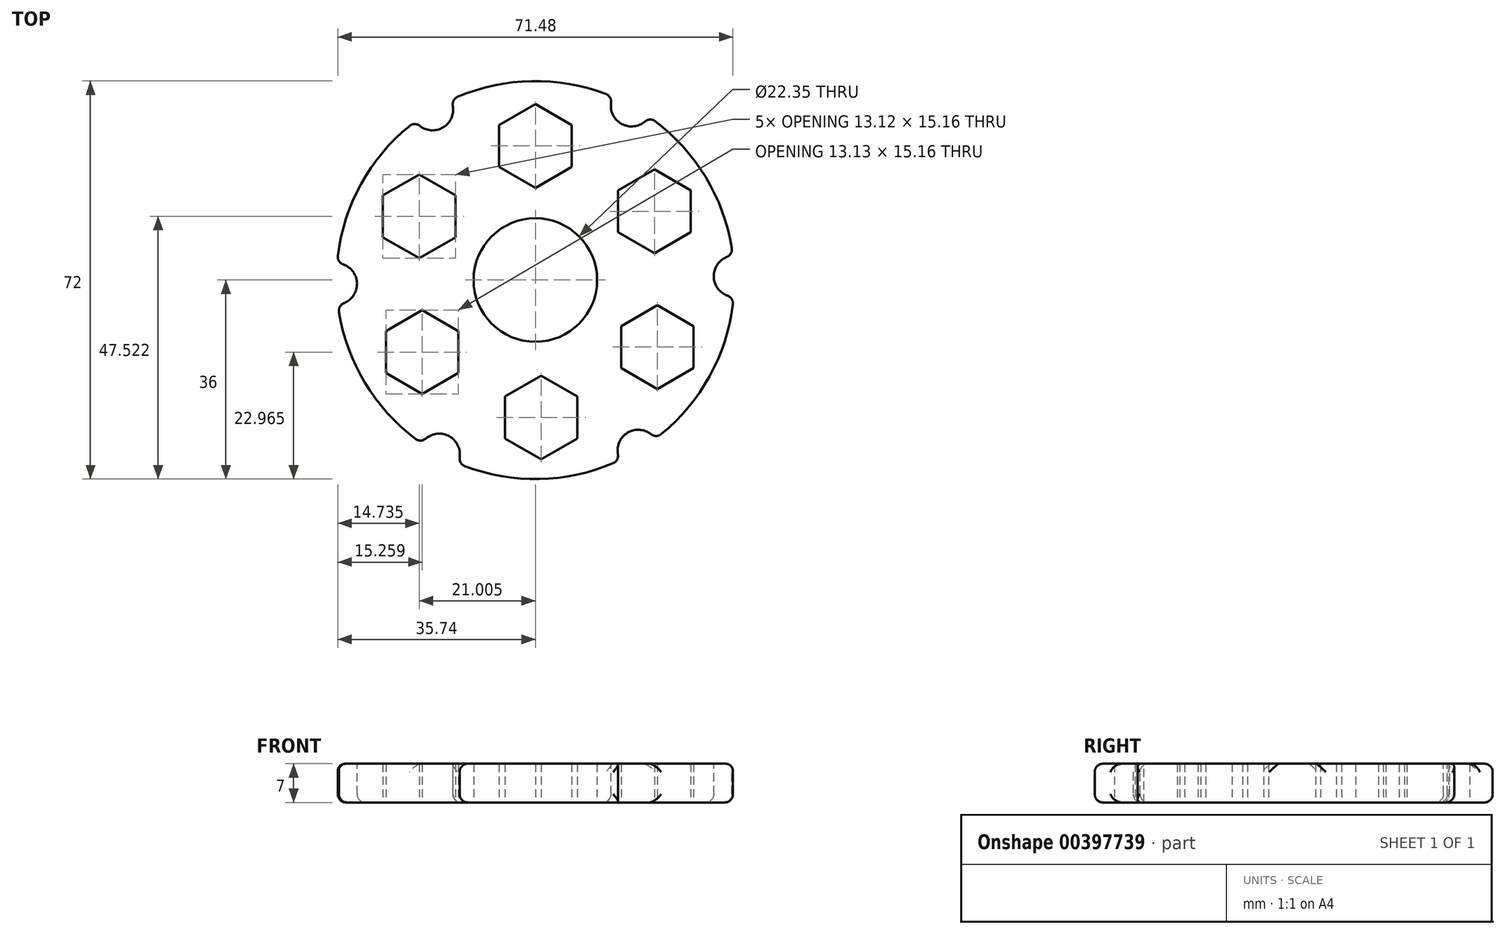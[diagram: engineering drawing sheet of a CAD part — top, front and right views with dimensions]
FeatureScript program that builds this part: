
annotation { "Feature Type Name" : "Feature", "Feature Type Description" : "" }
export const myFeature = defineFeature(function(context is Context, id is Id, definition is map)
    precondition{}
    {
        {
            var Q0;
            Q0=qCreatedBy(makeId("Top.planeOp"),FACE);
            var sketch = newSketch(context, id + "F0", { "sketchPlane" : qUnion([Q0])});
            skCircle(sketch, "E0", {"center": v(0, 0) * mm, "radius": 11.18 * mm});
            skCircle(sketch, "E1", {"center": v(0, 0) * mm, "radius": 36 * mm});
            skCircle(sketch, "E2.cCircle", {"center": v(0, 24.25) * mm, "radius": 6.56 * mm, "construction": true});
            skLineSegment(sketch, "E2.0", {"start": v(6.56, 28.04) * mm, "end": v(6.56, 20.47) * mm});
            skLineSegment(sketch, "E2.1", {"start": v(6.56, 20.47) * mm, "end": v(0, 16.68) * mm});
            skLineSegment(sketch, "E2.2", {"start": v(0, 16.68) * mm, "end": v(-6.56, 20.47) * mm});
            skLineSegment(sketch, "E2.3", {"start": v(-6.56, 20.47) * mm, "end": v(-6.56, 28.04) * mm});
            skLineSegment(sketch, "E2.4", {"start": v(-6.56, 28.04) * mm, "end": v(0, 31.83) * mm});
            skLineSegment(sketch, "E2.5", {"start": v(0, 31.83) * mm, "end": v(6.56, 28.04) * mm});
            skLineSegment(sketch, "E3.1.0", {"start": v(28.1, 8.64) * mm, "end": v(21.53, 4.85) * mm});
            skLineSegment(sketch, "E3.1.1", {"start": v(28.1, 16.22) * mm, "end": v(28.1, 8.64) * mm});
            skLineSegment(sketch, "E3.1.2", {"start": v(21.53, 20) * mm, "end": v(28.1, 16.22) * mm});
            skLineSegment(sketch, "E3.1.3", {"start": v(14.97, 16.22) * mm, "end": v(21.53, 20) * mm});
            skLineSegment(sketch, "E3.1.4", {"start": v(14.97, 8.64) * mm, "end": v(14.97, 16.22) * mm});
            skLineSegment(sketch, "E3.1.5", {"start": v(21.53, 4.85) * mm, "end": v(14.97, 8.64) * mm});
            skLineSegment(sketch, "E3.2.0", {"start": v(22.05, -19.7) * mm, "end": v(15.5, -15.92) * mm});
            skLineSegment(sketch, "E3.2.1", {"start": v(28.62, -15.92) * mm, "end": v(22.05, -19.7) * mm});
            skLineSegment(sketch, "E3.2.2", {"start": v(28.62, -8.34) * mm, "end": v(28.62, -15.92) * mm});
            skLineSegment(sketch, "E3.2.3", {"start": v(22.05, -4.55) * mm, "end": v(28.62, -8.34) * mm});
            skLineSegment(sketch, "E3.2.4", {"start": v(15.5, -8.34) * mm, "end": v(22.05, -4.55) * mm});
            skLineSegment(sketch, "E3.2.5", {"start": v(15.5, -15.92) * mm, "end": v(15.5, -8.34) * mm});
            skLineSegment(sketch, "E3.3.0", {"start": v(-5.51, -28.65) * mm, "end": v(-5.51, -21.07) * mm});
            skLineSegment(sketch, "E3.3.1", {"start": v(1.05, -32.44) * mm, "end": v(-5.51, -28.65) * mm});
            skLineSegment(sketch, "E3.3.2", {"start": v(7.61, -28.65) * mm, "end": v(1.05, -32.44) * mm});
            skLineSegment(sketch, "E3.3.3", {"start": v(7.61, -21.07) * mm, "end": v(7.61, -28.65) * mm});
            skLineSegment(sketch, "E3.3.4", {"start": v(1.05, -17.28) * mm, "end": v(7.61, -21.07) * mm});
            skLineSegment(sketch, "E3.3.5", {"start": v(-5.51, -21.07) * mm, "end": v(1.05, -17.28) * mm});
            skLineSegment(sketch, "E3.4.0", {"start": v(-27.04, -9.25) * mm, "end": v(-20.48, -5.46) * mm});
            skLineSegment(sketch, "E3.4.1", {"start": v(-27.04, -16.82) * mm, "end": v(-27.04, -9.25) * mm});
            skLineSegment(sketch, "E3.4.2", {"start": v(-20.48, -20.61) * mm, "end": v(-27.04, -16.82) * mm});
            skLineSegment(sketch, "E3.4.3", {"start": v(-13.92, -16.82) * mm, "end": v(-20.48, -20.61) * mm});
            skLineSegment(sketch, "E3.4.4", {"start": v(-13.92, -9.25) * mm, "end": v(-13.92, -16.82) * mm});
            skLineSegment(sketch, "E3.4.5", {"start": v(-20.48, -5.46) * mm, "end": v(-13.92, -9.25) * mm});
            skLineSegment(sketch, "E3.5.0", {"start": v(-21, 19.1) * mm, "end": v(-14.44, 15.31) * mm});
            skLineSegment(sketch, "E3.5.1", {"start": v(-27.57, 15.31) * mm, "end": v(-21, 19.1) * mm});
            skLineSegment(sketch, "E3.5.2", {"start": v(-27.57, 7.73) * mm, "end": v(-27.57, 15.31) * mm});
            skLineSegment(sketch, "E3.5.3", {"start": v(-21, 3.94) * mm, "end": v(-27.57, 7.73) * mm});
            skLineSegment(sketch, "E3.5.4", {"start": v(-14.44, 7.73) * mm, "end": v(-21, 3.94) * mm});
            skLineSegment(sketch, "E3.5.5", {"start": v(-14.44, 15.31) * mm, "end": v(-14.44, 7.73) * mm});
            skPoint(sketch, "E3.center", {"position": v(0.52, -0.3) * mm});
            skLineSegment(sketch, "E3.anchor1", {"start": v(0.52, -0.3) * mm, "end": v(6.56, 20.47) * mm, "construction": true});
            skLineSegment(sketch, "E3.anchor2", {"start": v(0.52, -0.3) * mm, "end": v(-14.44, 15.31) * mm, "construction": true});
            skSolve(sketch);
        }
        {
            var Q0;
            Q0=makeQuery(id+"F0.imprint","IMPRINT",FACE,{"disambiguationData":[TD([[makeQuery(id+"F0.imprint","IMPRINT",EDGE,{"derivedFrom":sQuery(id+"F0.wireOp",EDGE,"E0")}),-1.0]])]});
            extrude(context, id + "F1", {"entities" : qUnion([Q0]), "depth" : 7 * mm});
        }
        {
            var Q0;
            Q0=makeQuery(id+"F1.opExtrude","CAP_FACE",FACE,{"disambiguationData":[OSD([sQuery(id+"F0.wireOp",EDGE,"E0"),sQuery(id+"F0.wireOp",EDGE,"E1"),sQuery(id+"F0.wireOp",EDGE,"E2.0"),sQuery(id+"F0.wireOp",EDGE,"E2.1"),sQuery(id+"F0.wireOp",EDGE,"E2.2"),sQuery(id+"F0.wireOp",EDGE,"E2.3"),sQuery(id+"F0.wireOp",EDGE,"E2.4"),sQuery(id+"F0.wireOp",EDGE,"E2.5"),sQuery(id+"F0.wireOp",EDGE,"E3.1.0"),sQuery(id+"F0.wireOp",EDGE,"E3.1.1"),sQuery(id+"F0.wireOp",EDGE,"E3.1.2"),sQuery(id+"F0.wireOp",EDGE,"E3.1.3"),sQuery(id+"F0.wireOp",EDGE,"E3.1.4"),sQuery(id+"F0.wireOp",EDGE,"E3.1.5"),sQuery(id+"F0.wireOp",EDGE,"E3.2.0"),sQuery(id+"F0.wireOp",EDGE,"E3.2.1"),sQuery(id+"F0.wireOp",EDGE,"E3.2.2"),sQuery(id+"F0.wireOp",EDGE,"E3.2.3"),sQuery(id+"F0.wireOp",EDGE,"E3.2.4"),sQuery(id+"F0.wireOp",EDGE,"E3.2.5"),sQuery(id+"F0.wireOp",EDGE,"E3.3.0"),sQuery(id+"F0.wireOp",EDGE,"E3.3.1"),sQuery(id+"F0.wireOp",EDGE,"E3.3.2"),sQuery(id+"F0.wireOp",EDGE,"E3.3.3"),sQuery(id+"F0.wireOp",EDGE,"E3.3.4"),sQuery(id+"F0.wireOp",EDGE,"E3.3.5"),sQuery(id+"F0.wireOp",EDGE,"E3.4.0"),sQuery(id+"F0.wireOp",EDGE,"E3.4.1"),sQuery(id+"F0.wireOp",EDGE,"E3.4.2"),sQuery(id+"F0.wireOp",EDGE,"E3.4.3"),sQuery(id+"F0.wireOp",EDGE,"E3.4.4"),sQuery(id+"F0.wireOp",EDGE,"E3.4.5"),sQuery(id+"F0.wireOp",EDGE,"E3.5.0"),sQuery(id+"F0.wireOp",EDGE,"E3.5.1"),sQuery(id+"F0.wireOp",EDGE,"E3.5.2"),sQuery(id+"F0.wireOp",EDGE,"E3.5.3"),sQuery(id+"F0.wireOp",EDGE,"E3.5.4"),sQuery(id+"F0.wireOp",EDGE,"E3.5.5")])],"isStart":false});
            var sketch = newSketch(context, id + "F2", { "sketchPlane" : qUnion([Q0])});
            skCircle(sketch, "E4", {"center": v(17.4, 31.52) * mm, "radius": 3.73 * mm});
            skCircle(sketch, "E5.1.0", {"center": v(-18.6, 30.82) * mm, "radius": 3.73 * mm});
            skCircle(sketch, "E5.2.0", {"center": v(-36, -0.7) * mm, "radius": 3.73 * mm});
            skCircle(sketch, "E5.3.0", {"center": v(-17.4, -31.52) * mm, "radius": 3.73 * mm});
            skCircle(sketch, "E5.4.0", {"center": v(18.6, -30.82) * mm, "radius": 3.73 * mm});
            skCircle(sketch, "E5.5.0", {"center": v(36, 0.7) * mm, "radius": 3.73 * mm});
            skPoint(sketch, "E5.center", {"position": v(0, 0) * mm});
            skSolve(sketch);
        }
        {
            var Q0;
            {var subQ0=sQuery(id+"F2.wireOp",EDGE,"E5.1.0");var subQ1=makeQuery(id+"F1.opExtrude","CAP_EDGE",EDGE,{"disambiguationData":[OSD([sQuery(id+"F0.wireOp",EDGE,"E1")])],"isStart":false});var subQ2=makeQuery(id+"F2.imprint","INTERSECT",VERTEX,{"disambiguationData":[OD(0.0)],"derivedFrom":[subQ1,subQ0]});Q0=makeQuery(id+"F2.imprint","IMPRINT",FACE,{"disambiguationData":[TD([[makeQuery(id+"F2.imprint","IMPRINT",EDGE,{"disambiguationData":[TD([[subQ2,1.0]])],"derivedFrom":subQ0}),1.0]])]});}
            var Q1;
            {var subQ0=sQuery(id+"F2.wireOp",EDGE,"E5.1.0");var subQ1=makeQuery(id+"F1.opExtrude","CAP_EDGE",EDGE,{"disambiguationData":[OSD([sQuery(id+"F0.wireOp",EDGE,"E1")])],"isStart":false});var subQ2=makeQuery(id+"F2.imprint","INTERSECT",VERTEX,{"disambiguationData":[OD(0.0)],"derivedFrom":[subQ1,subQ0]});Q1=makeQuery(id+"F2.imprint","IMPRINT",FACE,{"disambiguationData":[TD([[makeQuery(id+"F2.imprint","IMPRINT",EDGE,{"disambiguationData":[TD([[subQ2,-1.0]])],"derivedFrom":subQ0}),1.0]])]});}
            var Q2;
            {var subQ0=sQuery(id+"F2.wireOp",EDGE,"E4");var subQ1=makeQuery(id+"F1.opExtrude","CAP_EDGE",EDGE,{"disambiguationData":[OSD([sQuery(id+"F0.wireOp",EDGE,"E1")])],"isStart":false});var subQ2=makeQuery(id+"F2.imprint","INTERSECT",VERTEX,{"disambiguationData":[OD(0.0)],"derivedFrom":[subQ1,subQ0]});Q2=makeQuery(id+"F2.imprint","IMPRINT",FACE,{"disambiguationData":[TD([[makeQuery(id+"F2.imprint","IMPRINT",EDGE,{"disambiguationData":[TD([[subQ2,1.0]])],"derivedFrom":subQ0}),1.0]])]});}
            var Q3;
            {var subQ0=sQuery(id+"F2.wireOp",EDGE,"E4");var subQ1=makeQuery(id+"F1.opExtrude","CAP_EDGE",EDGE,{"disambiguationData":[OSD([sQuery(id+"F0.wireOp",EDGE,"E1")])],"isStart":false});var subQ2=makeQuery(id+"F2.imprint","INTERSECT",VERTEX,{"disambiguationData":[OD(0.0)],"derivedFrom":[subQ1,subQ0]});Q3=makeQuery(id+"F2.imprint","IMPRINT",FACE,{"disambiguationData":[TD([[makeQuery(id+"F2.imprint","IMPRINT",EDGE,{"disambiguationData":[TD([[subQ2,-1.0]])],"derivedFrom":subQ0}),1.0]])]});}
            var Q4;
            {var subQ0=sQuery(id+"F2.wireOp",EDGE,"E5.5.0");var subQ1=makeQuery(id+"F1.opExtrude","CAP_EDGE",EDGE,{"disambiguationData":[OSD([sQuery(id+"F0.wireOp",EDGE,"E1")])],"isStart":false});var subQ2=makeQuery(id+"F2.imprint","INTERSECT",VERTEX,{"disambiguationData":[OD(0.0)],"derivedFrom":[subQ1,subQ0]});Q4=makeQuery(id+"F2.imprint","IMPRINT",FACE,{"disambiguationData":[TD([[makeQuery(id+"F2.imprint","IMPRINT",EDGE,{"disambiguationData":[TD([[subQ2,-1.0]])],"derivedFrom":subQ0}),1.0]])]});}
            var Q5;
            {var subQ0=sQuery(id+"F2.wireOp",EDGE,"E5.5.0");var subQ1=makeQuery(id+"F1.opExtrude","CAP_EDGE",EDGE,{"disambiguationData":[OSD([sQuery(id+"F0.wireOp",EDGE,"E1")])],"isStart":false});var subQ2=makeQuery(id+"F2.imprint","INTERSECT",VERTEX,{"disambiguationData":[OD(0.0)],"derivedFrom":[subQ1,subQ0]});Q5=makeQuery(id+"F2.imprint","IMPRINT",FACE,{"disambiguationData":[TD([[makeQuery(id+"F2.imprint","IMPRINT",EDGE,{"disambiguationData":[TD([[subQ2,1.0]])],"derivedFrom":subQ0}),1.0]])]});}
            var Q6;
            {var subQ0=sQuery(id+"F2.wireOp",EDGE,"E5.4.0");var subQ1=makeQuery(id+"F1.opExtrude","CAP_EDGE",EDGE,{"disambiguationData":[OSD([sQuery(id+"F0.wireOp",EDGE,"E1")])],"isStart":false});var subQ2=makeQuery(id+"F2.imprint","INTERSECT",VERTEX,{"disambiguationData":[OD(0.0)],"derivedFrom":[subQ1,subQ0]});Q6=makeQuery(id+"F2.imprint","IMPRINT",FACE,{"disambiguationData":[TD([[makeQuery(id+"F2.imprint","IMPRINT",EDGE,{"disambiguationData":[TD([[subQ2,-1.0]])],"derivedFrom":subQ0}),1.0]])]});}
            var Q7;
            {var subQ0=sQuery(id+"F2.wireOp",EDGE,"E5.4.0");var subQ1=makeQuery(id+"F1.opExtrude","CAP_EDGE",EDGE,{"disambiguationData":[OSD([sQuery(id+"F0.wireOp",EDGE,"E1")])],"isStart":false});var subQ2=makeQuery(id+"F2.imprint","INTERSECT",VERTEX,{"disambiguationData":[OD(0.0)],"derivedFrom":[subQ1,subQ0]});Q7=makeQuery(id+"F2.imprint","IMPRINT",FACE,{"disambiguationData":[TD([[makeQuery(id+"F2.imprint","IMPRINT",EDGE,{"disambiguationData":[TD([[subQ2,1.0]])],"derivedFrom":subQ0}),1.0]])]});}
            var Q8;
            {var subQ0=sQuery(id+"F2.wireOp",EDGE,"E5.3.0");var subQ1=makeQuery(id+"F1.opExtrude","CAP_EDGE",EDGE,{"disambiguationData":[OSD([sQuery(id+"F0.wireOp",EDGE,"E1")])],"isStart":false});var subQ2=makeQuery(id+"F2.imprint","INTERSECT",VERTEX,{"disambiguationData":[OD(0.0)],"derivedFrom":[subQ1,subQ0]});Q8=makeQuery(id+"F2.imprint","IMPRINT",FACE,{"disambiguationData":[TD([[makeQuery(id+"F2.imprint","IMPRINT",EDGE,{"disambiguationData":[TD([[subQ2,-1.0]])],"derivedFrom":subQ0}),1.0]])]});}
            var Q9;
            {var subQ0=sQuery(id+"F2.wireOp",EDGE,"E5.3.0");var subQ1=makeQuery(id+"F1.opExtrude","CAP_EDGE",EDGE,{"disambiguationData":[OSD([sQuery(id+"F0.wireOp",EDGE,"E1")])],"isStart":false});var subQ2=makeQuery(id+"F2.imprint","INTERSECT",VERTEX,{"disambiguationData":[OD(0.0)],"derivedFrom":[subQ1,subQ0]});Q9=makeQuery(id+"F2.imprint","IMPRINT",FACE,{"disambiguationData":[TD([[makeQuery(id+"F2.imprint","IMPRINT",EDGE,{"disambiguationData":[TD([[subQ2,1.0]])],"derivedFrom":subQ0}),1.0]])]});}
            var Q10;
            {var subQ0=sQuery(id+"F2.wireOp",EDGE,"E5.2.0");var subQ1=makeQuery(id+"F1.opExtrude","CAP_EDGE",EDGE,{"disambiguationData":[OSD([sQuery(id+"F0.wireOp",EDGE,"E1")])],"isStart":false});var subQ2=makeQuery(id+"F2.imprint","INTERSECT",VERTEX,{"disambiguationData":[OD(0.0)],"derivedFrom":[subQ1,subQ0]});Q10=makeQuery(id+"F2.imprint","IMPRINT",FACE,{"disambiguationData":[TD([[makeQuery(id+"F2.imprint","IMPRINT",EDGE,{"disambiguationData":[TD([[subQ2,1.0]])],"derivedFrom":subQ0}),1.0]])]});}
            var Q11;
            {var subQ0=sQuery(id+"F2.wireOp",EDGE,"E5.2.0");var subQ1=makeQuery(id+"F1.opExtrude","CAP_EDGE",EDGE,{"disambiguationData":[OSD([sQuery(id+"F0.wireOp",EDGE,"E1")])],"isStart":false});var subQ2=makeQuery(id+"F2.imprint","INTERSECT",VERTEX,{"disambiguationData":[OD(0.0)],"derivedFrom":[subQ1,subQ0]});Q11=makeQuery(id+"F2.imprint","IMPRINT",FACE,{"disambiguationData":[TD([[makeQuery(id+"F2.imprint","IMPRINT",EDGE,{"disambiguationData":[TD([[subQ2,-1.0]])],"derivedFrom":subQ0}),1.0]])]});}
            extrude(context, id + "F3", {"entities" : qUnion([Q0, Q1, Q2, Q3, Q4, Q5, Q6, Q7, Q8, Q9, Q10, Q11]), "operationType" : NewBodyOperationType.REMOVE, "oppositeDirection" : true, "depth" : 25 * mm});
        }
        {
            var Q0;
            {var subQ0=sQuery(id+"F0.wireOp",EDGE,"E1");Q0=makeQuery(id+"F3.boolean.opBoolean","SPLIT",EDGE,{"disambiguationData":[TD([makeQuery(id+"F1.opExtrude","CAP_FACE",FACE,{"disambiguationData":[OSD([sQuery(id+"F0.wireOp",EDGE,"E0"),subQ0,sQuery(id+"F0.wireOp",EDGE,"E2.0"),sQuery(id+"F0.wireOp",EDGE,"E2.1"),sQuery(id+"F0.wireOp",EDGE,"E2.2"),sQuery(id+"F0.wireOp",EDGE,"E2.3"),sQuery(id+"F0.wireOp",EDGE,"E2.4"),sQuery(id+"F0.wireOp",EDGE,"E2.5"),sQuery(id+"F0.wireOp",EDGE,"E3.1.0"),sQuery(id+"F0.wireOp",EDGE,"E3.1.1"),sQuery(id+"F0.wireOp",EDGE,"E3.1.2"),sQuery(id+"F0.wireOp",EDGE,"E3.1.3"),sQuery(id+"F0.wireOp",EDGE,"E3.1.4"),sQuery(id+"F0.wireOp",EDGE,"E3.1.5"),sQuery(id+"F0.wireOp",EDGE,"E3.2.0"),sQuery(id+"F0.wireOp",EDGE,"E3.2.1"),sQuery(id+"F0.wireOp",EDGE,"E3.2.2"),sQuery(id+"F0.wireOp",EDGE,"E3.2.3"),sQuery(id+"F0.wireOp",EDGE,"E3.2.4"),sQuery(id+"F0.wireOp",EDGE,"E3.2.5"),sQuery(id+"F0.wireOp",EDGE,"E3.3.0"),sQuery(id+"F0.wireOp",EDGE,"E3.3.1"),sQuery(id+"F0.wireOp",EDGE,"E3.3.2"),sQuery(id+"F0.wireOp",EDGE,"E3.3.3"),sQuery(id+"F0.wireOp",EDGE,"E3.3.4"),sQuery(id+"F0.wireOp",EDGE,"E3.3.5"),sQuery(id+"F0.wireOp",EDGE,"E3.4.0"),sQuery(id+"F0.wireOp",EDGE,"E3.4.1"),sQuery(id+"F0.wireOp",EDGE,"E3.4.2"),sQuery(id+"F0.wireOp",EDGE,"E3.4.3"),sQuery(id+"F0.wireOp",EDGE,"E3.4.4"),sQuery(id+"F0.wireOp",EDGE,"E3.4.5"),sQuery(id+"F0.wireOp",EDGE,"E3.5.0"),sQuery(id+"F0.wireOp",EDGE,"E3.5.1"),sQuery(id+"F0.wireOp",EDGE,"E3.5.2"),sQuery(id+"F0.wireOp",EDGE,"E3.5.3"),sQuery(id+"F0.wireOp",EDGE,"E3.5.4"),sQuery(id+"F0.wireOp",EDGE,"E3.5.5")])],"isStart":false}),makeQuery(id+"F1.opExtrude","SWEPT_FACE",FACE,{"disambiguationData":[OSD([subQ0])]}),makeQuery(id+"F3.opExtrude","SWEPT_FACE",FACE,{"disambiguationData":[OSD([sQuery(id+"F2.wireOp",EDGE,"E5.1.0")])]}),makeQuery(id+"F3.opExtrude","SWEPT_FACE",FACE,{"disambiguationData":[OSD([sQuery(id+"F2.wireOp",EDGE,"E5.2.0")])]})])],"derivedFrom":makeQuery(id+"F1.opExtrude","CAP_EDGE",EDGE,{"disambiguationData":[OSD([subQ0])],"isStart":false})});}
            var Q1;
            Q1=makeQuery(id+"F3.boolean.opBoolean","COPY",EDGE,{"derivedFrom":makeQuery(id+"F3.opExtrude","CAP_EDGE",EDGE,{"disambiguationData":[OSD([sQuery(id+"F2.wireOp",EDGE,"E5.1.0")])],"isStart":true})});
            var Q2;
            {var subQ0=sQuery(id+"F0.wireOp",EDGE,"E1");Q2=makeQuery(id+"F3.boolean.opBoolean","SPLIT",EDGE,{"disambiguationData":[TD([makeQuery(id+"F1.opExtrude","CAP_FACE",FACE,{"disambiguationData":[OSD([sQuery(id+"F0.wireOp",EDGE,"E0"),subQ0,sQuery(id+"F0.wireOp",EDGE,"E2.0"),sQuery(id+"F0.wireOp",EDGE,"E2.1"),sQuery(id+"F0.wireOp",EDGE,"E2.2"),sQuery(id+"F0.wireOp",EDGE,"E2.3"),sQuery(id+"F0.wireOp",EDGE,"E2.4"),sQuery(id+"F0.wireOp",EDGE,"E2.5"),sQuery(id+"F0.wireOp",EDGE,"E3.1.0"),sQuery(id+"F0.wireOp",EDGE,"E3.1.1"),sQuery(id+"F0.wireOp",EDGE,"E3.1.2"),sQuery(id+"F0.wireOp",EDGE,"E3.1.3"),sQuery(id+"F0.wireOp",EDGE,"E3.1.4"),sQuery(id+"F0.wireOp",EDGE,"E3.1.5"),sQuery(id+"F0.wireOp",EDGE,"E3.2.0"),sQuery(id+"F0.wireOp",EDGE,"E3.2.1"),sQuery(id+"F0.wireOp",EDGE,"E3.2.2"),sQuery(id+"F0.wireOp",EDGE,"E3.2.3"),sQuery(id+"F0.wireOp",EDGE,"E3.2.4"),sQuery(id+"F0.wireOp",EDGE,"E3.2.5"),sQuery(id+"F0.wireOp",EDGE,"E3.3.0"),sQuery(id+"F0.wireOp",EDGE,"E3.3.1"),sQuery(id+"F0.wireOp",EDGE,"E3.3.2"),sQuery(id+"F0.wireOp",EDGE,"E3.3.3"),sQuery(id+"F0.wireOp",EDGE,"E3.3.4"),sQuery(id+"F0.wireOp",EDGE,"E3.3.5"),sQuery(id+"F0.wireOp",EDGE,"E3.4.0"),sQuery(id+"F0.wireOp",EDGE,"E3.4.1"),sQuery(id+"F0.wireOp",EDGE,"E3.4.2"),sQuery(id+"F0.wireOp",EDGE,"E3.4.3"),sQuery(id+"F0.wireOp",EDGE,"E3.4.4"),sQuery(id+"F0.wireOp",EDGE,"E3.4.5"),sQuery(id+"F0.wireOp",EDGE,"E3.5.0"),sQuery(id+"F0.wireOp",EDGE,"E3.5.1"),sQuery(id+"F0.wireOp",EDGE,"E3.5.2"),sQuery(id+"F0.wireOp",EDGE,"E3.5.3"),sQuery(id+"F0.wireOp",EDGE,"E3.5.4"),sQuery(id+"F0.wireOp",EDGE,"E3.5.5")])],"isStart":false}),makeQuery(id+"F1.opExtrude","SWEPT_FACE",FACE,{"disambiguationData":[OSD([subQ0])]}),makeQuery(id+"F3.opExtrude","SWEPT_FACE",FACE,{"disambiguationData":[OSD([sQuery(id+"F2.wireOp",EDGE,"E4")])]}),makeQuery(id+"F3.opExtrude","SWEPT_FACE",FACE,{"disambiguationData":[OSD([sQuery(id+"F2.wireOp",EDGE,"E5.1.0")])]})])],"derivedFrom":makeQuery(id+"F1.opExtrude","CAP_EDGE",EDGE,{"disambiguationData":[OSD([subQ0])],"isStart":false})});}
            var Q3;
            Q3=makeQuery(id+"F3.boolean.opBoolean","COPY",EDGE,{"derivedFrom":makeQuery(id+"F3.opExtrude","CAP_EDGE",EDGE,{"disambiguationData":[OSD([sQuery(id+"F2.wireOp",EDGE,"E4")])],"isStart":true})});
            var Q4;
            {var subQ0=sQuery(id+"F0.wireOp",EDGE,"E1");Q4=makeQuery(id+"F3.boolean.opBoolean","SPLIT",EDGE,{"disambiguationData":[TD([makeQuery(id+"F1.opExtrude","CAP_FACE",FACE,{"disambiguationData":[OSD([sQuery(id+"F0.wireOp",EDGE,"E0"),subQ0,sQuery(id+"F0.wireOp",EDGE,"E2.0"),sQuery(id+"F0.wireOp",EDGE,"E2.1"),sQuery(id+"F0.wireOp",EDGE,"E2.2"),sQuery(id+"F0.wireOp",EDGE,"E2.3"),sQuery(id+"F0.wireOp",EDGE,"E2.4"),sQuery(id+"F0.wireOp",EDGE,"E2.5"),sQuery(id+"F0.wireOp",EDGE,"E3.1.0"),sQuery(id+"F0.wireOp",EDGE,"E3.1.1"),sQuery(id+"F0.wireOp",EDGE,"E3.1.2"),sQuery(id+"F0.wireOp",EDGE,"E3.1.3"),sQuery(id+"F0.wireOp",EDGE,"E3.1.4"),sQuery(id+"F0.wireOp",EDGE,"E3.1.5"),sQuery(id+"F0.wireOp",EDGE,"E3.2.0"),sQuery(id+"F0.wireOp",EDGE,"E3.2.1"),sQuery(id+"F0.wireOp",EDGE,"E3.2.2"),sQuery(id+"F0.wireOp",EDGE,"E3.2.3"),sQuery(id+"F0.wireOp",EDGE,"E3.2.4"),sQuery(id+"F0.wireOp",EDGE,"E3.2.5"),sQuery(id+"F0.wireOp",EDGE,"E3.3.0"),sQuery(id+"F0.wireOp",EDGE,"E3.3.1"),sQuery(id+"F0.wireOp",EDGE,"E3.3.2"),sQuery(id+"F0.wireOp",EDGE,"E3.3.3"),sQuery(id+"F0.wireOp",EDGE,"E3.3.4"),sQuery(id+"F0.wireOp",EDGE,"E3.3.5"),sQuery(id+"F0.wireOp",EDGE,"E3.4.0"),sQuery(id+"F0.wireOp",EDGE,"E3.4.1"),sQuery(id+"F0.wireOp",EDGE,"E3.4.2"),sQuery(id+"F0.wireOp",EDGE,"E3.4.3"),sQuery(id+"F0.wireOp",EDGE,"E3.4.4"),sQuery(id+"F0.wireOp",EDGE,"E3.4.5"),sQuery(id+"F0.wireOp",EDGE,"E3.5.0"),sQuery(id+"F0.wireOp",EDGE,"E3.5.1"),sQuery(id+"F0.wireOp",EDGE,"E3.5.2"),sQuery(id+"F0.wireOp",EDGE,"E3.5.3"),sQuery(id+"F0.wireOp",EDGE,"E3.5.4"),sQuery(id+"F0.wireOp",EDGE,"E3.5.5")])],"isStart":false}),makeQuery(id+"F1.opExtrude","SWEPT_FACE",FACE,{"disambiguationData":[OSD([subQ0])]}),makeQuery(id+"F3.opExtrude","SWEPT_FACE",FACE,{"disambiguationData":[OSD([sQuery(id+"F2.wireOp",EDGE,"E4")])]}),makeQuery(id+"F3.opExtrude","SWEPT_FACE",FACE,{"disambiguationData":[OSD([sQuery(id+"F2.wireOp",EDGE,"E5.5.0")])]})])],"derivedFrom":makeQuery(id+"F1.opExtrude","CAP_EDGE",EDGE,{"disambiguationData":[OSD([subQ0])],"isStart":false})});}
            var Q5;
            Q5=makeQuery(id+"F3.boolean.opBoolean","COPY",EDGE,{"derivedFrom":makeQuery(id+"F3.opExtrude","CAP_EDGE",EDGE,{"disambiguationData":[OSD([sQuery(id+"F2.wireOp",EDGE,"E5.5.0")])],"isStart":true})});
            var Q6;
            {var subQ0=sQuery(id+"F0.wireOp",EDGE,"E1");Q6=makeQuery(id+"F3.boolean.opBoolean","SPLIT",EDGE,{"disambiguationData":[TD([makeQuery(id+"F1.opExtrude","CAP_FACE",FACE,{"disambiguationData":[OSD([sQuery(id+"F0.wireOp",EDGE,"E0"),subQ0,sQuery(id+"F0.wireOp",EDGE,"E2.0"),sQuery(id+"F0.wireOp",EDGE,"E2.1"),sQuery(id+"F0.wireOp",EDGE,"E2.2"),sQuery(id+"F0.wireOp",EDGE,"E2.3"),sQuery(id+"F0.wireOp",EDGE,"E2.4"),sQuery(id+"F0.wireOp",EDGE,"E2.5"),sQuery(id+"F0.wireOp",EDGE,"E3.1.0"),sQuery(id+"F0.wireOp",EDGE,"E3.1.1"),sQuery(id+"F0.wireOp",EDGE,"E3.1.2"),sQuery(id+"F0.wireOp",EDGE,"E3.1.3"),sQuery(id+"F0.wireOp",EDGE,"E3.1.4"),sQuery(id+"F0.wireOp",EDGE,"E3.1.5"),sQuery(id+"F0.wireOp",EDGE,"E3.2.0"),sQuery(id+"F0.wireOp",EDGE,"E3.2.1"),sQuery(id+"F0.wireOp",EDGE,"E3.2.2"),sQuery(id+"F0.wireOp",EDGE,"E3.2.3"),sQuery(id+"F0.wireOp",EDGE,"E3.2.4"),sQuery(id+"F0.wireOp",EDGE,"E3.2.5"),sQuery(id+"F0.wireOp",EDGE,"E3.3.0"),sQuery(id+"F0.wireOp",EDGE,"E3.3.1"),sQuery(id+"F0.wireOp",EDGE,"E3.3.2"),sQuery(id+"F0.wireOp",EDGE,"E3.3.3"),sQuery(id+"F0.wireOp",EDGE,"E3.3.4"),sQuery(id+"F0.wireOp",EDGE,"E3.3.5"),sQuery(id+"F0.wireOp",EDGE,"E3.4.0"),sQuery(id+"F0.wireOp",EDGE,"E3.4.1"),sQuery(id+"F0.wireOp",EDGE,"E3.4.2"),sQuery(id+"F0.wireOp",EDGE,"E3.4.3"),sQuery(id+"F0.wireOp",EDGE,"E3.4.4"),sQuery(id+"F0.wireOp",EDGE,"E3.4.5"),sQuery(id+"F0.wireOp",EDGE,"E3.5.0"),sQuery(id+"F0.wireOp",EDGE,"E3.5.1"),sQuery(id+"F0.wireOp",EDGE,"E3.5.2"),sQuery(id+"F0.wireOp",EDGE,"E3.5.3"),sQuery(id+"F0.wireOp",EDGE,"E3.5.4"),sQuery(id+"F0.wireOp",EDGE,"E3.5.5")])],"isStart":false}),makeQuery(id+"F1.opExtrude","SWEPT_FACE",FACE,{"disambiguationData":[OSD([subQ0])]}),makeQuery(id+"F3.opExtrude","SWEPT_FACE",FACE,{"disambiguationData":[OSD([sQuery(id+"F2.wireOp",EDGE,"E5.4.0")])]}),makeQuery(id+"F3.opExtrude","SWEPT_FACE",FACE,{"disambiguationData":[OSD([sQuery(id+"F2.wireOp",EDGE,"E5.5.0")])]})])],"derivedFrom":makeQuery(id+"F1.opExtrude","CAP_EDGE",EDGE,{"disambiguationData":[OSD([subQ0])],"isStart":false})});}
            var Q7;
            Q7=makeQuery(id+"F3.boolean.opBoolean","COPY",EDGE,{"derivedFrom":makeQuery(id+"F3.opExtrude","CAP_EDGE",EDGE,{"disambiguationData":[OSD([sQuery(id+"F2.wireOp",EDGE,"E5.4.0")])],"isStart":true})});
            var Q8;
            {var subQ0=sQuery(id+"F0.wireOp",EDGE,"E1");Q8=makeQuery(id+"F3.boolean.opBoolean","SPLIT",EDGE,{"disambiguationData":[TD([makeQuery(id+"F1.opExtrude","CAP_FACE",FACE,{"disambiguationData":[OSD([sQuery(id+"F0.wireOp",EDGE,"E0"),subQ0,sQuery(id+"F0.wireOp",EDGE,"E2.0"),sQuery(id+"F0.wireOp",EDGE,"E2.1"),sQuery(id+"F0.wireOp",EDGE,"E2.2"),sQuery(id+"F0.wireOp",EDGE,"E2.3"),sQuery(id+"F0.wireOp",EDGE,"E2.4"),sQuery(id+"F0.wireOp",EDGE,"E2.5"),sQuery(id+"F0.wireOp",EDGE,"E3.1.0"),sQuery(id+"F0.wireOp",EDGE,"E3.1.1"),sQuery(id+"F0.wireOp",EDGE,"E3.1.2"),sQuery(id+"F0.wireOp",EDGE,"E3.1.3"),sQuery(id+"F0.wireOp",EDGE,"E3.1.4"),sQuery(id+"F0.wireOp",EDGE,"E3.1.5"),sQuery(id+"F0.wireOp",EDGE,"E3.2.0"),sQuery(id+"F0.wireOp",EDGE,"E3.2.1"),sQuery(id+"F0.wireOp",EDGE,"E3.2.2"),sQuery(id+"F0.wireOp",EDGE,"E3.2.3"),sQuery(id+"F0.wireOp",EDGE,"E3.2.4"),sQuery(id+"F0.wireOp",EDGE,"E3.2.5"),sQuery(id+"F0.wireOp",EDGE,"E3.3.0"),sQuery(id+"F0.wireOp",EDGE,"E3.3.1"),sQuery(id+"F0.wireOp",EDGE,"E3.3.2"),sQuery(id+"F0.wireOp",EDGE,"E3.3.3"),sQuery(id+"F0.wireOp",EDGE,"E3.3.4"),sQuery(id+"F0.wireOp",EDGE,"E3.3.5"),sQuery(id+"F0.wireOp",EDGE,"E3.4.0"),sQuery(id+"F0.wireOp",EDGE,"E3.4.1"),sQuery(id+"F0.wireOp",EDGE,"E3.4.2"),sQuery(id+"F0.wireOp",EDGE,"E3.4.3"),sQuery(id+"F0.wireOp",EDGE,"E3.4.4"),sQuery(id+"F0.wireOp",EDGE,"E3.4.5"),sQuery(id+"F0.wireOp",EDGE,"E3.5.0"),sQuery(id+"F0.wireOp",EDGE,"E3.5.1"),sQuery(id+"F0.wireOp",EDGE,"E3.5.2"),sQuery(id+"F0.wireOp",EDGE,"E3.5.3"),sQuery(id+"F0.wireOp",EDGE,"E3.5.4"),sQuery(id+"F0.wireOp",EDGE,"E3.5.5")])],"isStart":false}),makeQuery(id+"F1.opExtrude","SWEPT_FACE",FACE,{"disambiguationData":[OSD([subQ0])]}),makeQuery(id+"F3.opExtrude","SWEPT_FACE",FACE,{"disambiguationData":[OSD([sQuery(id+"F2.wireOp",EDGE,"E5.3.0")])]}),makeQuery(id+"F3.opExtrude","SWEPT_FACE",FACE,{"disambiguationData":[OSD([sQuery(id+"F2.wireOp",EDGE,"E5.4.0")])]})])],"derivedFrom":makeQuery(id+"F1.opExtrude","CAP_EDGE",EDGE,{"disambiguationData":[OSD([subQ0])],"isStart":false})});}
            var Q9;
            Q9=makeQuery(id+"F3.boolean.opBoolean","COPY",EDGE,{"derivedFrom":makeQuery(id+"F3.opExtrude","CAP_EDGE",EDGE,{"disambiguationData":[OSD([sQuery(id+"F2.wireOp",EDGE,"E5.3.0")])],"isStart":true})});
            var Q10;
            {var subQ0=sQuery(id+"F0.wireOp",EDGE,"E1");Q10=makeQuery(id+"F3.boolean.opBoolean","SPLIT",EDGE,{"disambiguationData":[TD([makeQuery(id+"F1.opExtrude","CAP_FACE",FACE,{"disambiguationData":[OSD([sQuery(id+"F0.wireOp",EDGE,"E0"),subQ0,sQuery(id+"F0.wireOp",EDGE,"E2.0"),sQuery(id+"F0.wireOp",EDGE,"E2.1"),sQuery(id+"F0.wireOp",EDGE,"E2.2"),sQuery(id+"F0.wireOp",EDGE,"E2.3"),sQuery(id+"F0.wireOp",EDGE,"E2.4"),sQuery(id+"F0.wireOp",EDGE,"E2.5"),sQuery(id+"F0.wireOp",EDGE,"E3.1.0"),sQuery(id+"F0.wireOp",EDGE,"E3.1.1"),sQuery(id+"F0.wireOp",EDGE,"E3.1.2"),sQuery(id+"F0.wireOp",EDGE,"E3.1.3"),sQuery(id+"F0.wireOp",EDGE,"E3.1.4"),sQuery(id+"F0.wireOp",EDGE,"E3.1.5"),sQuery(id+"F0.wireOp",EDGE,"E3.2.0"),sQuery(id+"F0.wireOp",EDGE,"E3.2.1"),sQuery(id+"F0.wireOp",EDGE,"E3.2.2"),sQuery(id+"F0.wireOp",EDGE,"E3.2.3"),sQuery(id+"F0.wireOp",EDGE,"E3.2.4"),sQuery(id+"F0.wireOp",EDGE,"E3.2.5"),sQuery(id+"F0.wireOp",EDGE,"E3.3.0"),sQuery(id+"F0.wireOp",EDGE,"E3.3.1"),sQuery(id+"F0.wireOp",EDGE,"E3.3.2"),sQuery(id+"F0.wireOp",EDGE,"E3.3.3"),sQuery(id+"F0.wireOp",EDGE,"E3.3.4"),sQuery(id+"F0.wireOp",EDGE,"E3.3.5"),sQuery(id+"F0.wireOp",EDGE,"E3.4.0"),sQuery(id+"F0.wireOp",EDGE,"E3.4.1"),sQuery(id+"F0.wireOp",EDGE,"E3.4.2"),sQuery(id+"F0.wireOp",EDGE,"E3.4.3"),sQuery(id+"F0.wireOp",EDGE,"E3.4.4"),sQuery(id+"F0.wireOp",EDGE,"E3.4.5"),sQuery(id+"F0.wireOp",EDGE,"E3.5.0"),sQuery(id+"F0.wireOp",EDGE,"E3.5.1"),sQuery(id+"F0.wireOp",EDGE,"E3.5.2"),sQuery(id+"F0.wireOp",EDGE,"E3.5.3"),sQuery(id+"F0.wireOp",EDGE,"E3.5.4"),sQuery(id+"F0.wireOp",EDGE,"E3.5.5")])],"isStart":false}),makeQuery(id+"F1.opExtrude","SWEPT_FACE",FACE,{"disambiguationData":[OSD([subQ0])]}),makeQuery(id+"F3.opExtrude","SWEPT_FACE",FACE,{"disambiguationData":[OSD([sQuery(id+"F2.wireOp",EDGE,"E5.2.0")])]}),makeQuery(id+"F3.opExtrude","SWEPT_FACE",FACE,{"disambiguationData":[OSD([sQuery(id+"F2.wireOp",EDGE,"E5.3.0")])]})])],"derivedFrom":makeQuery(id+"F1.opExtrude","CAP_EDGE",EDGE,{"disambiguationData":[OSD([subQ0])],"isStart":false})});}
            var Q11;
            Q11=makeQuery(id+"F3.boolean.opBoolean","COPY",EDGE,{"derivedFrom":makeQuery(id+"F3.opExtrude","CAP_EDGE",EDGE,{"disambiguationData":[OSD([sQuery(id+"F2.wireOp",EDGE,"E5.2.0")])],"isStart":true})});
            var Q12;
            {var subQ0=sQuery(id+"F0.wireOp",EDGE,"E1");Q12=makeQuery(id+"F3.boolean.opBoolean","SPLIT",EDGE,{"disambiguationData":[TD([makeQuery(id+"F1.opExtrude","CAP_FACE",FACE,{"disambiguationData":[OSD([sQuery(id+"F0.wireOp",EDGE,"E0"),subQ0,sQuery(id+"F0.wireOp",EDGE,"E2.0"),sQuery(id+"F0.wireOp",EDGE,"E2.1"),sQuery(id+"F0.wireOp",EDGE,"E2.2"),sQuery(id+"F0.wireOp",EDGE,"E2.3"),sQuery(id+"F0.wireOp",EDGE,"E2.4"),sQuery(id+"F0.wireOp",EDGE,"E2.5"),sQuery(id+"F0.wireOp",EDGE,"E3.1.0"),sQuery(id+"F0.wireOp",EDGE,"E3.1.1"),sQuery(id+"F0.wireOp",EDGE,"E3.1.2"),sQuery(id+"F0.wireOp",EDGE,"E3.1.3"),sQuery(id+"F0.wireOp",EDGE,"E3.1.4"),sQuery(id+"F0.wireOp",EDGE,"E3.1.5"),sQuery(id+"F0.wireOp",EDGE,"E3.2.0"),sQuery(id+"F0.wireOp",EDGE,"E3.2.1"),sQuery(id+"F0.wireOp",EDGE,"E3.2.2"),sQuery(id+"F0.wireOp",EDGE,"E3.2.3"),sQuery(id+"F0.wireOp",EDGE,"E3.2.4"),sQuery(id+"F0.wireOp",EDGE,"E3.2.5"),sQuery(id+"F0.wireOp",EDGE,"E3.3.0"),sQuery(id+"F0.wireOp",EDGE,"E3.3.1"),sQuery(id+"F0.wireOp",EDGE,"E3.3.2"),sQuery(id+"F0.wireOp",EDGE,"E3.3.3"),sQuery(id+"F0.wireOp",EDGE,"E3.3.4"),sQuery(id+"F0.wireOp",EDGE,"E3.3.5"),sQuery(id+"F0.wireOp",EDGE,"E3.4.0"),sQuery(id+"F0.wireOp",EDGE,"E3.4.1"),sQuery(id+"F0.wireOp",EDGE,"E3.4.2"),sQuery(id+"F0.wireOp",EDGE,"E3.4.3"),sQuery(id+"F0.wireOp",EDGE,"E3.4.4"),sQuery(id+"F0.wireOp",EDGE,"E3.4.5"),sQuery(id+"F0.wireOp",EDGE,"E3.5.0"),sQuery(id+"F0.wireOp",EDGE,"E3.5.1"),sQuery(id+"F0.wireOp",EDGE,"E3.5.2"),sQuery(id+"F0.wireOp",EDGE,"E3.5.3"),sQuery(id+"F0.wireOp",EDGE,"E3.5.4"),sQuery(id+"F0.wireOp",EDGE,"E3.5.5")])],"isStart":true}),makeQuery(id+"F1.opExtrude","SWEPT_FACE",FACE,{"disambiguationData":[OSD([subQ0])]}),makeQuery(id+"F3.opExtrude","SWEPT_FACE",FACE,{"disambiguationData":[OSD([sQuery(id+"F2.wireOp",EDGE,"E5.4.0")])]}),makeQuery(id+"F3.opExtrude","SWEPT_FACE",FACE,{"disambiguationData":[OSD([sQuery(id+"F2.wireOp",EDGE,"E5.5.0")])]})])],"derivedFrom":makeQuery(id+"F1.opExtrude","CAP_EDGE",EDGE,{"disambiguationData":[OSD([subQ0])],"isStart":true})});}
            var Q13;
            Q13=makeQuery(id+"F3.boolean.opBoolean","INTERSECT",EDGE,{"derivedFrom":[makeQuery(id+"F1.opExtrude","CAP_FACE",FACE,{"disambiguationData":[OSD([sQuery(id+"F0.wireOp",EDGE,"E0"),sQuery(id+"F0.wireOp",EDGE,"E1"),sQuery(id+"F0.wireOp",EDGE,"E2.0"),sQuery(id+"F0.wireOp",EDGE,"E2.1"),sQuery(id+"F0.wireOp",EDGE,"E2.2"),sQuery(id+"F0.wireOp",EDGE,"E2.3"),sQuery(id+"F0.wireOp",EDGE,"E2.4"),sQuery(id+"F0.wireOp",EDGE,"E2.5"),sQuery(id+"F0.wireOp",EDGE,"E3.1.0"),sQuery(id+"F0.wireOp",EDGE,"E3.1.1"),sQuery(id+"F0.wireOp",EDGE,"E3.1.2"),sQuery(id+"F0.wireOp",EDGE,"E3.1.3"),sQuery(id+"F0.wireOp",EDGE,"E3.1.4"),sQuery(id+"F0.wireOp",EDGE,"E3.1.5"),sQuery(id+"F0.wireOp",EDGE,"E3.2.0"),sQuery(id+"F0.wireOp",EDGE,"E3.2.1"),sQuery(id+"F0.wireOp",EDGE,"E3.2.2"),sQuery(id+"F0.wireOp",EDGE,"E3.2.3"),sQuery(id+"F0.wireOp",EDGE,"E3.2.4"),sQuery(id+"F0.wireOp",EDGE,"E3.2.5"),sQuery(id+"F0.wireOp",EDGE,"E3.3.0"),sQuery(id+"F0.wireOp",EDGE,"E3.3.1"),sQuery(id+"F0.wireOp",EDGE,"E3.3.2"),sQuery(id+"F0.wireOp",EDGE,"E3.3.3"),sQuery(id+"F0.wireOp",EDGE,"E3.3.4"),sQuery(id+"F0.wireOp",EDGE,"E3.3.5"),sQuery(id+"F0.wireOp",EDGE,"E3.4.0"),sQuery(id+"F0.wireOp",EDGE,"E3.4.1"),sQuery(id+"F0.wireOp",EDGE,"E3.4.2"),sQuery(id+"F0.wireOp",EDGE,"E3.4.3"),sQuery(id+"F0.wireOp",EDGE,"E3.4.4"),sQuery(id+"F0.wireOp",EDGE,"E3.4.5"),sQuery(id+"F0.wireOp",EDGE,"E3.5.0"),sQuery(id+"F0.wireOp",EDGE,"E3.5.1"),sQuery(id+"F0.wireOp",EDGE,"E3.5.2"),sQuery(id+"F0.wireOp",EDGE,"E3.5.3"),sQuery(id+"F0.wireOp",EDGE,"E3.5.4"),sQuery(id+"F0.wireOp",EDGE,"E3.5.5")])],"isStart":true}),makeQuery(id+"F3.opExtrude","SWEPT_FACE",FACE,{"disambiguationData":[OSD([sQuery(id+"F2.wireOp",EDGE,"E5.5.0")])]})]});
            var Q14;
            {var subQ0=sQuery(id+"F0.wireOp",EDGE,"E1");Q14=makeQuery(id+"F3.boolean.opBoolean","SPLIT",EDGE,{"disambiguationData":[TD([makeQuery(id+"F1.opExtrude","CAP_FACE",FACE,{"disambiguationData":[OSD([sQuery(id+"F0.wireOp",EDGE,"E0"),subQ0,sQuery(id+"F0.wireOp",EDGE,"E2.0"),sQuery(id+"F0.wireOp",EDGE,"E2.1"),sQuery(id+"F0.wireOp",EDGE,"E2.2"),sQuery(id+"F0.wireOp",EDGE,"E2.3"),sQuery(id+"F0.wireOp",EDGE,"E2.4"),sQuery(id+"F0.wireOp",EDGE,"E2.5"),sQuery(id+"F0.wireOp",EDGE,"E3.1.0"),sQuery(id+"F0.wireOp",EDGE,"E3.1.1"),sQuery(id+"F0.wireOp",EDGE,"E3.1.2"),sQuery(id+"F0.wireOp",EDGE,"E3.1.3"),sQuery(id+"F0.wireOp",EDGE,"E3.1.4"),sQuery(id+"F0.wireOp",EDGE,"E3.1.5"),sQuery(id+"F0.wireOp",EDGE,"E3.2.0"),sQuery(id+"F0.wireOp",EDGE,"E3.2.1"),sQuery(id+"F0.wireOp",EDGE,"E3.2.2"),sQuery(id+"F0.wireOp",EDGE,"E3.2.3"),sQuery(id+"F0.wireOp",EDGE,"E3.2.4"),sQuery(id+"F0.wireOp",EDGE,"E3.2.5"),sQuery(id+"F0.wireOp",EDGE,"E3.3.0"),sQuery(id+"F0.wireOp",EDGE,"E3.3.1"),sQuery(id+"F0.wireOp",EDGE,"E3.3.2"),sQuery(id+"F0.wireOp",EDGE,"E3.3.3"),sQuery(id+"F0.wireOp",EDGE,"E3.3.4"),sQuery(id+"F0.wireOp",EDGE,"E3.3.5"),sQuery(id+"F0.wireOp",EDGE,"E3.4.0"),sQuery(id+"F0.wireOp",EDGE,"E3.4.1"),sQuery(id+"F0.wireOp",EDGE,"E3.4.2"),sQuery(id+"F0.wireOp",EDGE,"E3.4.3"),sQuery(id+"F0.wireOp",EDGE,"E3.4.4"),sQuery(id+"F0.wireOp",EDGE,"E3.4.5"),sQuery(id+"F0.wireOp",EDGE,"E3.5.0"),sQuery(id+"F0.wireOp",EDGE,"E3.5.1"),sQuery(id+"F0.wireOp",EDGE,"E3.5.2"),sQuery(id+"F0.wireOp",EDGE,"E3.5.3"),sQuery(id+"F0.wireOp",EDGE,"E3.5.4"),sQuery(id+"F0.wireOp",EDGE,"E3.5.5")])],"isStart":true}),makeQuery(id+"F1.opExtrude","SWEPT_FACE",FACE,{"disambiguationData":[OSD([subQ0])]}),makeQuery(id+"F3.opExtrude","SWEPT_FACE",FACE,{"disambiguationData":[OSD([sQuery(id+"F2.wireOp",EDGE,"E4")])]}),makeQuery(id+"F3.opExtrude","SWEPT_FACE",FACE,{"disambiguationData":[OSD([sQuery(id+"F2.wireOp",EDGE,"E5.5.0")])]})])],"derivedFrom":makeQuery(id+"F1.opExtrude","CAP_EDGE",EDGE,{"disambiguationData":[OSD([subQ0])],"isStart":true})});}
            var Q15;
            Q15=makeQuery(id+"F3.boolean.opBoolean","INTERSECT",EDGE,{"derivedFrom":[makeQuery(id+"F1.opExtrude","CAP_FACE",FACE,{"disambiguationData":[OSD([sQuery(id+"F0.wireOp",EDGE,"E0"),sQuery(id+"F0.wireOp",EDGE,"E1"),sQuery(id+"F0.wireOp",EDGE,"E2.0"),sQuery(id+"F0.wireOp",EDGE,"E2.1"),sQuery(id+"F0.wireOp",EDGE,"E2.2"),sQuery(id+"F0.wireOp",EDGE,"E2.3"),sQuery(id+"F0.wireOp",EDGE,"E2.4"),sQuery(id+"F0.wireOp",EDGE,"E2.5"),sQuery(id+"F0.wireOp",EDGE,"E3.1.0"),sQuery(id+"F0.wireOp",EDGE,"E3.1.1"),sQuery(id+"F0.wireOp",EDGE,"E3.1.2"),sQuery(id+"F0.wireOp",EDGE,"E3.1.3"),sQuery(id+"F0.wireOp",EDGE,"E3.1.4"),sQuery(id+"F0.wireOp",EDGE,"E3.1.5"),sQuery(id+"F0.wireOp",EDGE,"E3.2.0"),sQuery(id+"F0.wireOp",EDGE,"E3.2.1"),sQuery(id+"F0.wireOp",EDGE,"E3.2.2"),sQuery(id+"F0.wireOp",EDGE,"E3.2.3"),sQuery(id+"F0.wireOp",EDGE,"E3.2.4"),sQuery(id+"F0.wireOp",EDGE,"E3.2.5"),sQuery(id+"F0.wireOp",EDGE,"E3.3.0"),sQuery(id+"F0.wireOp",EDGE,"E3.3.1"),sQuery(id+"F0.wireOp",EDGE,"E3.3.2"),sQuery(id+"F0.wireOp",EDGE,"E3.3.3"),sQuery(id+"F0.wireOp",EDGE,"E3.3.4"),sQuery(id+"F0.wireOp",EDGE,"E3.3.5"),sQuery(id+"F0.wireOp",EDGE,"E3.4.0"),sQuery(id+"F0.wireOp",EDGE,"E3.4.1"),sQuery(id+"F0.wireOp",EDGE,"E3.4.2"),sQuery(id+"F0.wireOp",EDGE,"E3.4.3"),sQuery(id+"F0.wireOp",EDGE,"E3.4.4"),sQuery(id+"F0.wireOp",EDGE,"E3.4.5"),sQuery(id+"F0.wireOp",EDGE,"E3.5.0"),sQuery(id+"F0.wireOp",EDGE,"E3.5.1"),sQuery(id+"F0.wireOp",EDGE,"E3.5.2"),sQuery(id+"F0.wireOp",EDGE,"E3.5.3"),sQuery(id+"F0.wireOp",EDGE,"E3.5.4"),sQuery(id+"F0.wireOp",EDGE,"E3.5.5")])],"isStart":true}),makeQuery(id+"F3.opExtrude","SWEPT_FACE",FACE,{"disambiguationData":[OSD([sQuery(id+"F2.wireOp",EDGE,"E4")])]})]});
            var Q16;
            {var subQ0=sQuery(id+"F0.wireOp",EDGE,"E1");Q16=makeQuery(id+"F3.boolean.opBoolean","SPLIT",EDGE,{"disambiguationData":[TD([makeQuery(id+"F1.opExtrude","CAP_FACE",FACE,{"disambiguationData":[OSD([sQuery(id+"F0.wireOp",EDGE,"E0"),subQ0,sQuery(id+"F0.wireOp",EDGE,"E2.0"),sQuery(id+"F0.wireOp",EDGE,"E2.1"),sQuery(id+"F0.wireOp",EDGE,"E2.2"),sQuery(id+"F0.wireOp",EDGE,"E2.3"),sQuery(id+"F0.wireOp",EDGE,"E2.4"),sQuery(id+"F0.wireOp",EDGE,"E2.5"),sQuery(id+"F0.wireOp",EDGE,"E3.1.0"),sQuery(id+"F0.wireOp",EDGE,"E3.1.1"),sQuery(id+"F0.wireOp",EDGE,"E3.1.2"),sQuery(id+"F0.wireOp",EDGE,"E3.1.3"),sQuery(id+"F0.wireOp",EDGE,"E3.1.4"),sQuery(id+"F0.wireOp",EDGE,"E3.1.5"),sQuery(id+"F0.wireOp",EDGE,"E3.2.0"),sQuery(id+"F0.wireOp",EDGE,"E3.2.1"),sQuery(id+"F0.wireOp",EDGE,"E3.2.2"),sQuery(id+"F0.wireOp",EDGE,"E3.2.3"),sQuery(id+"F0.wireOp",EDGE,"E3.2.4"),sQuery(id+"F0.wireOp",EDGE,"E3.2.5"),sQuery(id+"F0.wireOp",EDGE,"E3.3.0"),sQuery(id+"F0.wireOp",EDGE,"E3.3.1"),sQuery(id+"F0.wireOp",EDGE,"E3.3.2"),sQuery(id+"F0.wireOp",EDGE,"E3.3.3"),sQuery(id+"F0.wireOp",EDGE,"E3.3.4"),sQuery(id+"F0.wireOp",EDGE,"E3.3.5"),sQuery(id+"F0.wireOp",EDGE,"E3.4.0"),sQuery(id+"F0.wireOp",EDGE,"E3.4.1"),sQuery(id+"F0.wireOp",EDGE,"E3.4.2"),sQuery(id+"F0.wireOp",EDGE,"E3.4.3"),sQuery(id+"F0.wireOp",EDGE,"E3.4.4"),sQuery(id+"F0.wireOp",EDGE,"E3.4.5"),sQuery(id+"F0.wireOp",EDGE,"E3.5.0"),sQuery(id+"F0.wireOp",EDGE,"E3.5.1"),sQuery(id+"F0.wireOp",EDGE,"E3.5.2"),sQuery(id+"F0.wireOp",EDGE,"E3.5.3"),sQuery(id+"F0.wireOp",EDGE,"E3.5.4"),sQuery(id+"F0.wireOp",EDGE,"E3.5.5")])],"isStart":true}),makeQuery(id+"F1.opExtrude","SWEPT_FACE",FACE,{"disambiguationData":[OSD([subQ0])]}),makeQuery(id+"F3.opExtrude","SWEPT_FACE",FACE,{"disambiguationData":[OSD([sQuery(id+"F2.wireOp",EDGE,"E4")])]}),makeQuery(id+"F3.opExtrude","SWEPT_FACE",FACE,{"disambiguationData":[OSD([sQuery(id+"F2.wireOp",EDGE,"E5.1.0")])]})])],"derivedFrom":makeQuery(id+"F1.opExtrude","CAP_EDGE",EDGE,{"disambiguationData":[OSD([subQ0])],"isStart":true})});}
            var Q17;
            Q17=makeQuery(id+"F3.boolean.opBoolean","INTERSECT",EDGE,{"derivedFrom":[makeQuery(id+"F1.opExtrude","CAP_FACE",FACE,{"disambiguationData":[OSD([sQuery(id+"F0.wireOp",EDGE,"E0"),sQuery(id+"F0.wireOp",EDGE,"E1"),sQuery(id+"F0.wireOp",EDGE,"E2.0"),sQuery(id+"F0.wireOp",EDGE,"E2.1"),sQuery(id+"F0.wireOp",EDGE,"E2.2"),sQuery(id+"F0.wireOp",EDGE,"E2.3"),sQuery(id+"F0.wireOp",EDGE,"E2.4"),sQuery(id+"F0.wireOp",EDGE,"E2.5"),sQuery(id+"F0.wireOp",EDGE,"E3.1.0"),sQuery(id+"F0.wireOp",EDGE,"E3.1.1"),sQuery(id+"F0.wireOp",EDGE,"E3.1.2"),sQuery(id+"F0.wireOp",EDGE,"E3.1.3"),sQuery(id+"F0.wireOp",EDGE,"E3.1.4"),sQuery(id+"F0.wireOp",EDGE,"E3.1.5"),sQuery(id+"F0.wireOp",EDGE,"E3.2.0"),sQuery(id+"F0.wireOp",EDGE,"E3.2.1"),sQuery(id+"F0.wireOp",EDGE,"E3.2.2"),sQuery(id+"F0.wireOp",EDGE,"E3.2.3"),sQuery(id+"F0.wireOp",EDGE,"E3.2.4"),sQuery(id+"F0.wireOp",EDGE,"E3.2.5"),sQuery(id+"F0.wireOp",EDGE,"E3.3.0"),sQuery(id+"F0.wireOp",EDGE,"E3.3.1"),sQuery(id+"F0.wireOp",EDGE,"E3.3.2"),sQuery(id+"F0.wireOp",EDGE,"E3.3.3"),sQuery(id+"F0.wireOp",EDGE,"E3.3.4"),sQuery(id+"F0.wireOp",EDGE,"E3.3.5"),sQuery(id+"F0.wireOp",EDGE,"E3.4.0"),sQuery(id+"F0.wireOp",EDGE,"E3.4.1"),sQuery(id+"F0.wireOp",EDGE,"E3.4.2"),sQuery(id+"F0.wireOp",EDGE,"E3.4.3"),sQuery(id+"F0.wireOp",EDGE,"E3.4.4"),sQuery(id+"F0.wireOp",EDGE,"E3.4.5"),sQuery(id+"F0.wireOp",EDGE,"E3.5.0"),sQuery(id+"F0.wireOp",EDGE,"E3.5.1"),sQuery(id+"F0.wireOp",EDGE,"E3.5.2"),sQuery(id+"F0.wireOp",EDGE,"E3.5.3"),sQuery(id+"F0.wireOp",EDGE,"E3.5.4"),sQuery(id+"F0.wireOp",EDGE,"E3.5.5")])],"isStart":true}),makeQuery(id+"F3.opExtrude","SWEPT_FACE",FACE,{"disambiguationData":[OSD([sQuery(id+"F2.wireOp",EDGE,"E5.1.0")])]})]});
            var Q18;
            {var subQ0=sQuery(id+"F0.wireOp",EDGE,"E1");Q18=makeQuery(id+"F3.boolean.opBoolean","SPLIT",EDGE,{"disambiguationData":[TD([makeQuery(id+"F1.opExtrude","CAP_FACE",FACE,{"disambiguationData":[OSD([sQuery(id+"F0.wireOp",EDGE,"E0"),subQ0,sQuery(id+"F0.wireOp",EDGE,"E2.0"),sQuery(id+"F0.wireOp",EDGE,"E2.1"),sQuery(id+"F0.wireOp",EDGE,"E2.2"),sQuery(id+"F0.wireOp",EDGE,"E2.3"),sQuery(id+"F0.wireOp",EDGE,"E2.4"),sQuery(id+"F0.wireOp",EDGE,"E2.5"),sQuery(id+"F0.wireOp",EDGE,"E3.1.0"),sQuery(id+"F0.wireOp",EDGE,"E3.1.1"),sQuery(id+"F0.wireOp",EDGE,"E3.1.2"),sQuery(id+"F0.wireOp",EDGE,"E3.1.3"),sQuery(id+"F0.wireOp",EDGE,"E3.1.4"),sQuery(id+"F0.wireOp",EDGE,"E3.1.5"),sQuery(id+"F0.wireOp",EDGE,"E3.2.0"),sQuery(id+"F0.wireOp",EDGE,"E3.2.1"),sQuery(id+"F0.wireOp",EDGE,"E3.2.2"),sQuery(id+"F0.wireOp",EDGE,"E3.2.3"),sQuery(id+"F0.wireOp",EDGE,"E3.2.4"),sQuery(id+"F0.wireOp",EDGE,"E3.2.5"),sQuery(id+"F0.wireOp",EDGE,"E3.3.0"),sQuery(id+"F0.wireOp",EDGE,"E3.3.1"),sQuery(id+"F0.wireOp",EDGE,"E3.3.2"),sQuery(id+"F0.wireOp",EDGE,"E3.3.3"),sQuery(id+"F0.wireOp",EDGE,"E3.3.4"),sQuery(id+"F0.wireOp",EDGE,"E3.3.5"),sQuery(id+"F0.wireOp",EDGE,"E3.4.0"),sQuery(id+"F0.wireOp",EDGE,"E3.4.1"),sQuery(id+"F0.wireOp",EDGE,"E3.4.2"),sQuery(id+"F0.wireOp",EDGE,"E3.4.3"),sQuery(id+"F0.wireOp",EDGE,"E3.4.4"),sQuery(id+"F0.wireOp",EDGE,"E3.4.5"),sQuery(id+"F0.wireOp",EDGE,"E3.5.0"),sQuery(id+"F0.wireOp",EDGE,"E3.5.1"),sQuery(id+"F0.wireOp",EDGE,"E3.5.2"),sQuery(id+"F0.wireOp",EDGE,"E3.5.3"),sQuery(id+"F0.wireOp",EDGE,"E3.5.4"),sQuery(id+"F0.wireOp",EDGE,"E3.5.5")])],"isStart":true}),makeQuery(id+"F1.opExtrude","SWEPT_FACE",FACE,{"disambiguationData":[OSD([subQ0])]}),makeQuery(id+"F3.opExtrude","SWEPT_FACE",FACE,{"disambiguationData":[OSD([sQuery(id+"F2.wireOp",EDGE,"E5.1.0")])]}),makeQuery(id+"F3.opExtrude","SWEPT_FACE",FACE,{"disambiguationData":[OSD([sQuery(id+"F2.wireOp",EDGE,"E5.2.0")])]})])],"derivedFrom":makeQuery(id+"F1.opExtrude","CAP_EDGE",EDGE,{"disambiguationData":[OSD([subQ0])],"isStart":true})});}
            var Q19;
            Q19=makeQuery(id+"F3.boolean.opBoolean","INTERSECT",EDGE,{"derivedFrom":[makeQuery(id+"F1.opExtrude","CAP_FACE",FACE,{"disambiguationData":[OSD([sQuery(id+"F0.wireOp",EDGE,"E0"),sQuery(id+"F0.wireOp",EDGE,"E1"),sQuery(id+"F0.wireOp",EDGE,"E2.0"),sQuery(id+"F0.wireOp",EDGE,"E2.1"),sQuery(id+"F0.wireOp",EDGE,"E2.2"),sQuery(id+"F0.wireOp",EDGE,"E2.3"),sQuery(id+"F0.wireOp",EDGE,"E2.4"),sQuery(id+"F0.wireOp",EDGE,"E2.5"),sQuery(id+"F0.wireOp",EDGE,"E3.1.0"),sQuery(id+"F0.wireOp",EDGE,"E3.1.1"),sQuery(id+"F0.wireOp",EDGE,"E3.1.2"),sQuery(id+"F0.wireOp",EDGE,"E3.1.3"),sQuery(id+"F0.wireOp",EDGE,"E3.1.4"),sQuery(id+"F0.wireOp",EDGE,"E3.1.5"),sQuery(id+"F0.wireOp",EDGE,"E3.2.0"),sQuery(id+"F0.wireOp",EDGE,"E3.2.1"),sQuery(id+"F0.wireOp",EDGE,"E3.2.2"),sQuery(id+"F0.wireOp",EDGE,"E3.2.3"),sQuery(id+"F0.wireOp",EDGE,"E3.2.4"),sQuery(id+"F0.wireOp",EDGE,"E3.2.5"),sQuery(id+"F0.wireOp",EDGE,"E3.3.0"),sQuery(id+"F0.wireOp",EDGE,"E3.3.1"),sQuery(id+"F0.wireOp",EDGE,"E3.3.2"),sQuery(id+"F0.wireOp",EDGE,"E3.3.3"),sQuery(id+"F0.wireOp",EDGE,"E3.3.4"),sQuery(id+"F0.wireOp",EDGE,"E3.3.5"),sQuery(id+"F0.wireOp",EDGE,"E3.4.0"),sQuery(id+"F0.wireOp",EDGE,"E3.4.1"),sQuery(id+"F0.wireOp",EDGE,"E3.4.2"),sQuery(id+"F0.wireOp",EDGE,"E3.4.3"),sQuery(id+"F0.wireOp",EDGE,"E3.4.4"),sQuery(id+"F0.wireOp",EDGE,"E3.4.5"),sQuery(id+"F0.wireOp",EDGE,"E3.5.0"),sQuery(id+"F0.wireOp",EDGE,"E3.5.1"),sQuery(id+"F0.wireOp",EDGE,"E3.5.2"),sQuery(id+"F0.wireOp",EDGE,"E3.5.3"),sQuery(id+"F0.wireOp",EDGE,"E3.5.4"),sQuery(id+"F0.wireOp",EDGE,"E3.5.5")])],"isStart":true}),makeQuery(id+"F3.opExtrude","SWEPT_FACE",FACE,{"disambiguationData":[OSD([sQuery(id+"F2.wireOp",EDGE,"E5.2.0")])]})]});
            var Q20;
            {var subQ0=sQuery(id+"F0.wireOp",EDGE,"E1");Q20=makeQuery(id+"F3.boolean.opBoolean","SPLIT",EDGE,{"disambiguationData":[TD([makeQuery(id+"F1.opExtrude","CAP_FACE",FACE,{"disambiguationData":[OSD([sQuery(id+"F0.wireOp",EDGE,"E0"),subQ0,sQuery(id+"F0.wireOp",EDGE,"E2.0"),sQuery(id+"F0.wireOp",EDGE,"E2.1"),sQuery(id+"F0.wireOp",EDGE,"E2.2"),sQuery(id+"F0.wireOp",EDGE,"E2.3"),sQuery(id+"F0.wireOp",EDGE,"E2.4"),sQuery(id+"F0.wireOp",EDGE,"E2.5"),sQuery(id+"F0.wireOp",EDGE,"E3.1.0"),sQuery(id+"F0.wireOp",EDGE,"E3.1.1"),sQuery(id+"F0.wireOp",EDGE,"E3.1.2"),sQuery(id+"F0.wireOp",EDGE,"E3.1.3"),sQuery(id+"F0.wireOp",EDGE,"E3.1.4"),sQuery(id+"F0.wireOp",EDGE,"E3.1.5"),sQuery(id+"F0.wireOp",EDGE,"E3.2.0"),sQuery(id+"F0.wireOp",EDGE,"E3.2.1"),sQuery(id+"F0.wireOp",EDGE,"E3.2.2"),sQuery(id+"F0.wireOp",EDGE,"E3.2.3"),sQuery(id+"F0.wireOp",EDGE,"E3.2.4"),sQuery(id+"F0.wireOp",EDGE,"E3.2.5"),sQuery(id+"F0.wireOp",EDGE,"E3.3.0"),sQuery(id+"F0.wireOp",EDGE,"E3.3.1"),sQuery(id+"F0.wireOp",EDGE,"E3.3.2"),sQuery(id+"F0.wireOp",EDGE,"E3.3.3"),sQuery(id+"F0.wireOp",EDGE,"E3.3.4"),sQuery(id+"F0.wireOp",EDGE,"E3.3.5"),sQuery(id+"F0.wireOp",EDGE,"E3.4.0"),sQuery(id+"F0.wireOp",EDGE,"E3.4.1"),sQuery(id+"F0.wireOp",EDGE,"E3.4.2"),sQuery(id+"F0.wireOp",EDGE,"E3.4.3"),sQuery(id+"F0.wireOp",EDGE,"E3.4.4"),sQuery(id+"F0.wireOp",EDGE,"E3.4.5"),sQuery(id+"F0.wireOp",EDGE,"E3.5.0"),sQuery(id+"F0.wireOp",EDGE,"E3.5.1"),sQuery(id+"F0.wireOp",EDGE,"E3.5.2"),sQuery(id+"F0.wireOp",EDGE,"E3.5.3"),sQuery(id+"F0.wireOp",EDGE,"E3.5.4"),sQuery(id+"F0.wireOp",EDGE,"E3.5.5")])],"isStart":true}),makeQuery(id+"F1.opExtrude","SWEPT_FACE",FACE,{"disambiguationData":[OSD([subQ0])]}),makeQuery(id+"F3.opExtrude","SWEPT_FACE",FACE,{"disambiguationData":[OSD([sQuery(id+"F2.wireOp",EDGE,"E5.2.0")])]}),makeQuery(id+"F3.opExtrude","SWEPT_FACE",FACE,{"disambiguationData":[OSD([sQuery(id+"F2.wireOp",EDGE,"E5.3.0")])]})])],"derivedFrom":makeQuery(id+"F1.opExtrude","CAP_EDGE",EDGE,{"disambiguationData":[OSD([subQ0])],"isStart":true})});}
            var Q21;
            Q21=makeQuery(id+"F3.boolean.opBoolean","INTERSECT",EDGE,{"derivedFrom":[makeQuery(id+"F1.opExtrude","CAP_FACE",FACE,{"disambiguationData":[OSD([sQuery(id+"F0.wireOp",EDGE,"E0"),sQuery(id+"F0.wireOp",EDGE,"E1"),sQuery(id+"F0.wireOp",EDGE,"E2.0"),sQuery(id+"F0.wireOp",EDGE,"E2.1"),sQuery(id+"F0.wireOp",EDGE,"E2.2"),sQuery(id+"F0.wireOp",EDGE,"E2.3"),sQuery(id+"F0.wireOp",EDGE,"E2.4"),sQuery(id+"F0.wireOp",EDGE,"E2.5"),sQuery(id+"F0.wireOp",EDGE,"E3.1.0"),sQuery(id+"F0.wireOp",EDGE,"E3.1.1"),sQuery(id+"F0.wireOp",EDGE,"E3.1.2"),sQuery(id+"F0.wireOp",EDGE,"E3.1.3"),sQuery(id+"F0.wireOp",EDGE,"E3.1.4"),sQuery(id+"F0.wireOp",EDGE,"E3.1.5"),sQuery(id+"F0.wireOp",EDGE,"E3.2.0"),sQuery(id+"F0.wireOp",EDGE,"E3.2.1"),sQuery(id+"F0.wireOp",EDGE,"E3.2.2"),sQuery(id+"F0.wireOp",EDGE,"E3.2.3"),sQuery(id+"F0.wireOp",EDGE,"E3.2.4"),sQuery(id+"F0.wireOp",EDGE,"E3.2.5"),sQuery(id+"F0.wireOp",EDGE,"E3.3.0"),sQuery(id+"F0.wireOp",EDGE,"E3.3.1"),sQuery(id+"F0.wireOp",EDGE,"E3.3.2"),sQuery(id+"F0.wireOp",EDGE,"E3.3.3"),sQuery(id+"F0.wireOp",EDGE,"E3.3.4"),sQuery(id+"F0.wireOp",EDGE,"E3.3.5"),sQuery(id+"F0.wireOp",EDGE,"E3.4.0"),sQuery(id+"F0.wireOp",EDGE,"E3.4.1"),sQuery(id+"F0.wireOp",EDGE,"E3.4.2"),sQuery(id+"F0.wireOp",EDGE,"E3.4.3"),sQuery(id+"F0.wireOp",EDGE,"E3.4.4"),sQuery(id+"F0.wireOp",EDGE,"E3.4.5"),sQuery(id+"F0.wireOp",EDGE,"E3.5.0"),sQuery(id+"F0.wireOp",EDGE,"E3.5.1"),sQuery(id+"F0.wireOp",EDGE,"E3.5.2"),sQuery(id+"F0.wireOp",EDGE,"E3.5.3"),sQuery(id+"F0.wireOp",EDGE,"E3.5.4"),sQuery(id+"F0.wireOp",EDGE,"E3.5.5")])],"isStart":true}),makeQuery(id+"F3.opExtrude","SWEPT_FACE",FACE,{"disambiguationData":[OSD([sQuery(id+"F2.wireOp",EDGE,"E5.3.0")])]})]});
            var Q22;
            {var subQ0=sQuery(id+"F0.wireOp",EDGE,"E1");Q22=makeQuery(id+"F3.boolean.opBoolean","SPLIT",EDGE,{"disambiguationData":[TD([makeQuery(id+"F1.opExtrude","CAP_FACE",FACE,{"disambiguationData":[OSD([sQuery(id+"F0.wireOp",EDGE,"E0"),subQ0,sQuery(id+"F0.wireOp",EDGE,"E2.0"),sQuery(id+"F0.wireOp",EDGE,"E2.1"),sQuery(id+"F0.wireOp",EDGE,"E2.2"),sQuery(id+"F0.wireOp",EDGE,"E2.3"),sQuery(id+"F0.wireOp",EDGE,"E2.4"),sQuery(id+"F0.wireOp",EDGE,"E2.5"),sQuery(id+"F0.wireOp",EDGE,"E3.1.0"),sQuery(id+"F0.wireOp",EDGE,"E3.1.1"),sQuery(id+"F0.wireOp",EDGE,"E3.1.2"),sQuery(id+"F0.wireOp",EDGE,"E3.1.3"),sQuery(id+"F0.wireOp",EDGE,"E3.1.4"),sQuery(id+"F0.wireOp",EDGE,"E3.1.5"),sQuery(id+"F0.wireOp",EDGE,"E3.2.0"),sQuery(id+"F0.wireOp",EDGE,"E3.2.1"),sQuery(id+"F0.wireOp",EDGE,"E3.2.2"),sQuery(id+"F0.wireOp",EDGE,"E3.2.3"),sQuery(id+"F0.wireOp",EDGE,"E3.2.4"),sQuery(id+"F0.wireOp",EDGE,"E3.2.5"),sQuery(id+"F0.wireOp",EDGE,"E3.3.0"),sQuery(id+"F0.wireOp",EDGE,"E3.3.1"),sQuery(id+"F0.wireOp",EDGE,"E3.3.2"),sQuery(id+"F0.wireOp",EDGE,"E3.3.3"),sQuery(id+"F0.wireOp",EDGE,"E3.3.4"),sQuery(id+"F0.wireOp",EDGE,"E3.3.5"),sQuery(id+"F0.wireOp",EDGE,"E3.4.0"),sQuery(id+"F0.wireOp",EDGE,"E3.4.1"),sQuery(id+"F0.wireOp",EDGE,"E3.4.2"),sQuery(id+"F0.wireOp",EDGE,"E3.4.3"),sQuery(id+"F0.wireOp",EDGE,"E3.4.4"),sQuery(id+"F0.wireOp",EDGE,"E3.4.5"),sQuery(id+"F0.wireOp",EDGE,"E3.5.0"),sQuery(id+"F0.wireOp",EDGE,"E3.5.1"),sQuery(id+"F0.wireOp",EDGE,"E3.5.2"),sQuery(id+"F0.wireOp",EDGE,"E3.5.3"),sQuery(id+"F0.wireOp",EDGE,"E3.5.4"),sQuery(id+"F0.wireOp",EDGE,"E3.5.5")])],"isStart":true}),makeQuery(id+"F1.opExtrude","SWEPT_FACE",FACE,{"disambiguationData":[OSD([subQ0])]}),makeQuery(id+"F3.opExtrude","SWEPT_FACE",FACE,{"disambiguationData":[OSD([sQuery(id+"F2.wireOp",EDGE,"E5.3.0")])]}),makeQuery(id+"F3.opExtrude","SWEPT_FACE",FACE,{"disambiguationData":[OSD([sQuery(id+"F2.wireOp",EDGE,"E5.4.0")])]})])],"derivedFrom":makeQuery(id+"F1.opExtrude","CAP_EDGE",EDGE,{"disambiguationData":[OSD([subQ0])],"isStart":true})});}
            var Q23;
            Q23=makeQuery(id+"F3.boolean.opBoolean","INTERSECT",EDGE,{"disambiguationData":[OD(1.0)],"derivedFrom":[makeQuery(id+"F1.opExtrude","SWEPT_FACE",FACE,{"disambiguationData":[OSD([sQuery(id+"F0.wireOp",EDGE,"E1")])]}),makeQuery(id+"F3.opExtrude","SWEPT_FACE",FACE,{"disambiguationData":[OSD([sQuery(id+"F2.wireOp",EDGE,"E4")])]})]});
            var Q24;
            Q24=makeQuery(id+"F3.boolean.opBoolean","INTERSECT",EDGE,{"disambiguationData":[OD(0.0)],"derivedFrom":[makeQuery(id+"F1.opExtrude","SWEPT_FACE",FACE,{"disambiguationData":[OSD([sQuery(id+"F0.wireOp",EDGE,"E1")])]}),makeQuery(id+"F3.opExtrude","SWEPT_FACE",FACE,{"disambiguationData":[OSD([sQuery(id+"F2.wireOp",EDGE,"E4")])]})]});
            var Q25;
            Q25=makeQuery(id+"F3.boolean.opBoolean","INTERSECT",EDGE,{"disambiguationData":[OD(0.0)],"derivedFrom":[makeQuery(id+"F1.opExtrude","SWEPT_FACE",FACE,{"disambiguationData":[OSD([sQuery(id+"F0.wireOp",EDGE,"E1")])]}),makeQuery(id+"F3.opExtrude","SWEPT_FACE",FACE,{"disambiguationData":[OSD([sQuery(id+"F2.wireOp",EDGE,"E5.1.0")])]})]});
            var Q26;
            {var subQ0=sQuery(id+"F0.wireOp",EDGE,"E3.5.5");var subQ1=sQuery(id+"F0.wireOp",EDGE,"E3.5.4");var subQ2=sQuery(id+"F0.wireOp",EDGE,"E3.5.3");var subQ3=sQuery(id+"F0.wireOp",EDGE,"E3.5.2");var subQ4=sQuery(id+"F0.wireOp",EDGE,"E3.5.1");var subQ5=sQuery(id+"F0.wireOp",EDGE,"E3.5.0");var subQ6=sQuery(id+"F0.wireOp",EDGE,"E3.4.5");var subQ7=sQuery(id+"F0.wireOp",EDGE,"E3.4.4");var subQ8=sQuery(id+"F0.wireOp",EDGE,"E3.4.3");var subQ9=sQuery(id+"F0.wireOp",EDGE,"E3.4.2");var subQ10=sQuery(id+"F0.wireOp",EDGE,"E3.4.1");var subQ11=sQuery(id+"F0.wireOp",EDGE,"E3.4.0");var subQ12=sQuery(id+"F0.wireOp",EDGE,"E3.3.5");var subQ13=sQuery(id+"F0.wireOp",EDGE,"E3.3.4");var subQ14=sQuery(id+"F0.wireOp",EDGE,"E3.3.3");var subQ15=sQuery(id+"F0.wireOp",EDGE,"E3.3.2");var subQ16=sQuery(id+"F0.wireOp",EDGE,"E3.3.1");var subQ17=sQuery(id+"F0.wireOp",EDGE,"E3.3.0");var subQ18=sQuery(id+"F0.wireOp",EDGE,"E3.2.5");var subQ19=sQuery(id+"F0.wireOp",EDGE,"E3.2.4");var subQ20=sQuery(id+"F0.wireOp",EDGE,"E3.2.3");var subQ21=sQuery(id+"F0.wireOp",EDGE,"E3.2.2");var subQ22=sQuery(id+"F0.wireOp",EDGE,"E3.2.1");var subQ23=sQuery(id+"F0.wireOp",EDGE,"E3.2.0");var subQ24=sQuery(id+"F0.wireOp",EDGE,"E3.1.5");var subQ25=sQuery(id+"F0.wireOp",EDGE,"E3.1.4");var subQ26=sQuery(id+"F0.wireOp",EDGE,"E3.1.3");var subQ27=sQuery(id+"F0.wireOp",EDGE,"E3.1.2");var subQ28=sQuery(id+"F0.wireOp",EDGE,"E3.1.1");var subQ29=sQuery(id+"F0.wireOp",EDGE,"E3.1.0");var subQ30=sQuery(id+"F0.wireOp",EDGE,"E2.5");var subQ31=sQuery(id+"F0.wireOp",EDGE,"E2.4");var subQ32=sQuery(id+"F0.wireOp",EDGE,"E2.3");var subQ33=sQuery(id+"F0.wireOp",EDGE,"E2.2");var subQ34=sQuery(id+"F0.wireOp",EDGE,"E2.1");var subQ35=sQuery(id+"F0.wireOp",EDGE,"E2.0");var subQ36=sQuery(id+"F0.wireOp",EDGE,"E1");var subQ37=sQuery(id+"F0.wireOp",EDGE,"E0");Q26=makeQuery(id+"F3.boolean.opBoolean","SPLIT",FACE,{"disambiguationData":[TD([makeQuery(id+"F1.opExtrude","CAP_FACE",FACE,{"disambiguationData":[OSD([subQ37,subQ36,subQ35,subQ34,subQ33,subQ32,subQ31,subQ30,subQ29,subQ28,subQ27,subQ26,subQ25,subQ24,subQ23,subQ22,subQ21,subQ20,subQ19,subQ18,subQ17,subQ16,subQ15,subQ14,subQ13,subQ12,subQ11,subQ10,subQ9,subQ8,subQ7,subQ6,subQ5,subQ4,subQ3,subQ2,subQ1,subQ0])],"isStart":true}),makeQuery(id+"F1.opExtrude","CAP_FACE",FACE,{"disambiguationData":[OSD([subQ37,subQ36,subQ35,subQ34,subQ33,subQ32,subQ31,subQ30,subQ29,subQ28,subQ27,subQ26,subQ25,subQ24,subQ23,subQ22,subQ21,subQ20,subQ19,subQ18,subQ17,subQ16,subQ15,subQ14,subQ13,subQ12,subQ11,subQ10,subQ9,subQ8,subQ7,subQ6,subQ5,subQ4,subQ3,subQ2,subQ1,subQ0])],"isStart":false}),makeQuery(id+"F3.opExtrude","SWEPT_FACE",FACE,{"disambiguationData":[OSD([sQuery(id+"F2.wireOp",EDGE,"E5.1.0")])]}),makeQuery(id+"F3.opExtrude","SWEPT_FACE",FACE,{"disambiguationData":[OSD([sQuery(id+"F2.wireOp",EDGE,"E5.2.0")])]})])],"derivedFrom":makeQuery(id+"F1.opExtrude","SWEPT_FACE",FACE,{"disambiguationData":[OSD([subQ36])]})});}
            var Q27;
            Q27=makeQuery(id+"F3.boolean.opBoolean","INTERSECT",EDGE,{"disambiguationData":[OD(1.0)],"derivedFrom":[makeQuery(id+"F1.opExtrude","SWEPT_FACE",FACE,{"disambiguationData":[OSD([sQuery(id+"F0.wireOp",EDGE,"E1")])]}),makeQuery(id+"F3.opExtrude","SWEPT_FACE",FACE,{"disambiguationData":[OSD([sQuery(id+"F2.wireOp",EDGE,"E5.2.0")])]})]});
            var Q28;
            Q28=makeQuery(id+"F3.boolean.opBoolean","INTERSECT",EDGE,{"disambiguationData":[OD(0.0)],"derivedFrom":[makeQuery(id+"F1.opExtrude","SWEPT_FACE",FACE,{"disambiguationData":[OSD([sQuery(id+"F0.wireOp",EDGE,"E1")])]}),makeQuery(id+"F3.opExtrude","SWEPT_FACE",FACE,{"disambiguationData":[OSD([sQuery(id+"F2.wireOp",EDGE,"E5.2.0")])]})]});
            var Q29;
            Q29=makeQuery(id+"F3.boolean.opBoolean","INTERSECT",EDGE,{"disambiguationData":[OD(1.0)],"derivedFrom":[makeQuery(id+"F1.opExtrude","SWEPT_FACE",FACE,{"disambiguationData":[OSD([sQuery(id+"F0.wireOp",EDGE,"E1")])]}),makeQuery(id+"F3.opExtrude","SWEPT_FACE",FACE,{"disambiguationData":[OSD([sQuery(id+"F2.wireOp",EDGE,"E5.3.0")])]})]});
            var Q30;
            Q30=makeQuery(id+"F3.boolean.opBoolean","COPY",FACE,{"derivedFrom":makeQuery(id+"F3.opExtrude","SWEPT_FACE",FACE,{"disambiguationData":[OSD([sQuery(id+"F2.wireOp",EDGE,"E5.3.0")])]})});
            var Q31;
            Q31=makeQuery(id+"F3.boolean.opBoolean","INTERSECT",EDGE,{"disambiguationData":[OD(0.0)],"derivedFrom":[makeQuery(id+"F1.opExtrude","SWEPT_FACE",FACE,{"disambiguationData":[OSD([sQuery(id+"F0.wireOp",EDGE,"E1")])]}),makeQuery(id+"F3.opExtrude","SWEPT_FACE",FACE,{"disambiguationData":[OSD([sQuery(id+"F2.wireOp",EDGE,"E5.4.0")])]})]});
            var Q32;
            Q32=makeQuery(id+"F3.boolean.opBoolean","INTERSECT",EDGE,{"disambiguationData":[OD(1.0)],"derivedFrom":[makeQuery(id+"F1.opExtrude","SWEPT_FACE",FACE,{"disambiguationData":[OSD([sQuery(id+"F0.wireOp",EDGE,"E1")])]}),makeQuery(id+"F3.opExtrude","SWEPT_FACE",FACE,{"disambiguationData":[OSD([sQuery(id+"F2.wireOp",EDGE,"E5.4.0")])]})]});
            var Q33;
            Q33=makeQuery(id+"F3.boolean.opBoolean","INTERSECT",EDGE,{"disambiguationData":[OD(1.0)],"derivedFrom":[makeQuery(id+"F1.opExtrude","SWEPT_FACE",FACE,{"disambiguationData":[OSD([sQuery(id+"F0.wireOp",EDGE,"E1")])]}),makeQuery(id+"F3.opExtrude","SWEPT_FACE",FACE,{"disambiguationData":[OSD([sQuery(id+"F2.wireOp",EDGE,"E5.5.0")])]})]});
            var Q34;
            Q34=makeQuery(id+"F3.boolean.opBoolean","INTERSECT",EDGE,{"disambiguationData":[OD(0.0)],"derivedFrom":[makeQuery(id+"F1.opExtrude","SWEPT_FACE",FACE,{"disambiguationData":[OSD([sQuery(id+"F0.wireOp",EDGE,"E1")])]}),makeQuery(id+"F3.opExtrude","SWEPT_FACE",FACE,{"disambiguationData":[OSD([sQuery(id+"F2.wireOp",EDGE,"E5.5.0")])]})]});
            fillet(context, id + "F4", {"entities" : qUnion([Q0, Q1, Q2, Q3, Q4, Q5, Q6, Q7, Q8, Q9, Q10, Q11, Q12, Q13, Q14, Q15, Q16, Q17, Q18, Q19, Q20, Q21, Q22, Q23, Q24, Q25, Q26, Q27, Q28, Q29, Q30, Q31, Q32, Q33, Q34]), "radius" : 1.5 * mm, "tangentPropagation" : true, "allowEdgeOverflow" : false});
        }
    });
